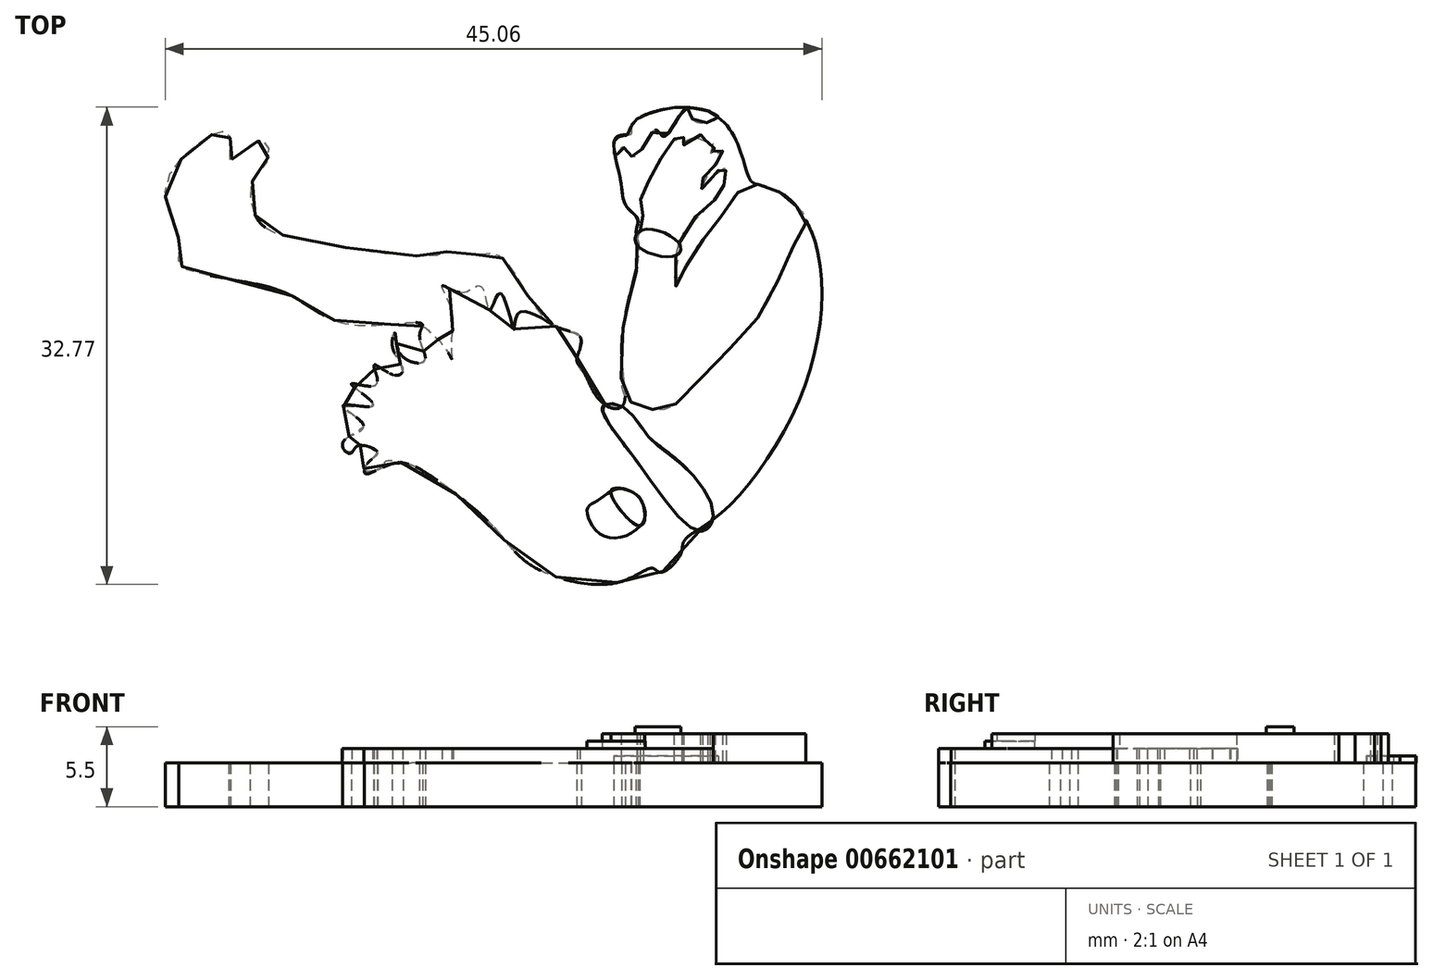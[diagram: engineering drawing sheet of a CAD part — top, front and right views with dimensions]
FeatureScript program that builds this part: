
annotation { "Feature Type Name" : "Feature", "Feature Type Description" : "" }
export const myFeature = defineFeature(function(context is Context, id is Id, definition is map)
    precondition{}
    {
        {
            var Q0;
            Q0=qCreatedBy(makeId("Top.planeOp"),FACE);
            var sketch = newSketch(context, id + "F0", { "sketchPlane" : qUnion([Q0])});
            skFitSpline(sketch, "E0", {"points": [v(-29.16, 38) * mm, v(-28.15, 38.22) * mm, v(-28.09, 38.84) * mm, v(-24.81, 40.03) * mm, v(-21.54, 38.73) * mm, v(-20.24, 35.68) * mm, v(-19.73, 34.83) * mm, v(-17.87, 34.15) * mm, v(-15.38, 30.26) * mm, v(-16.5, 20.2) * mm, v(-22.38, 11.84) * mm, v(-24.53, 10.26) * mm, v(-24.76, 9.36) * mm, v(-26.11, 8.11) * mm, v(-26.68, 8.4) * mm, v(-29, 7.44) * mm, v(-34.87, 8.5) * mm, v(-37.47, 11.1) * mm, v(-41.87, 14.72) * mm, v(-44.53, 15.57) * mm, v(-46.39, 14.9) * mm, v(-46.16, 15.68) * mm, v(-45.54, 16.36) * mm, v(-46.9, 16.81) * mm, v(-47.3, 16.36) * mm, v(-47.69, 16.36) * mm, v(-47.86, 17.15) * mm, v(-46.5, 18.17) * mm, v(-47.91, 19.58) * mm, v(-45.82, 19.58) * mm, v(-47.35, 21.05) * mm, v(-45.66, 21) * mm, v(-45.77, 22.35) * mm, v(-44.53, 21.67) * mm, v(-43.8, 22) * mm, v(-44.53, 23.6) * mm, v(-44.36, 24.55) * mm, v(-43.96, 23.08) * mm, v(-42.32, 22.63) * mm, v(-42.66, 24.38) * mm, v(-42.5, 25.17) * mm, v(-47.46, 25.12) * mm, v(-52.32, 27.49) * mm, v(-58.99, 29.13) * mm, v(-59.15, 30.76) * mm, v(-60.12, 34.38) * mm, v(-58.08, 37.37) * mm, v(-56.22, 38.39) * mm, v(-55.65, 37.94) * mm, v(-55.7, 36.47) * mm, v(-54.3, 37.43) * mm, v(-53.22, 37.65) * mm, v(-53.17, 36.24) * mm, v(-54.18, 34.89) * mm, v(-53.79, 32.35) * mm, v(-50.85, 30.99) * mm, v(-41.7, 29.86) * mm, v(-40.74, 30.14) * mm, v(-38.88, 29.92) * mm, v(-37.3, 29.92) * mm, v(-34.98, 26.7) * mm, v(-33.06, 24.89) * mm, v(-31.6, 24.16) * mm, v(-31.87, 22.69) * mm, v(-31.53, 22.12) * mm, v(-30.4, 20.03) * mm, v(-29.1, 19.35) * mm, v(-28.6, 19.86) * mm, v(-28.77, 24.21) * mm, v(-27.58, 30.42) * mm, v(-27.8, 31.5) * mm, v(-27.7, 32.35) * mm, v(-28.48, 33.25) * mm, v(-28.88, 35.06) * mm, v(-29.16, 38) * mm]});
            skSolve(sketch);
        }
        {
            var Q0;
            Q0 = qSketchRegion(id + "F0", true);
            extrude(context, id + "F1", {"entities" : qUnion([Q0]), "depth" : 3 * mm, "offsetDistance" : 25 * mm});
        }
        {
            var Q0;
            Q0=makeQuery(id+"F1.opExtrude","CAP_FACE",FACE,{"disambiguationData":[OSD([sQuery(id+"F0.wireOp",EDGE,"E0")])],"isStart":false});
            var sketch = newSketch(context, id + "F2", { "sketchPlane" : qUnion([Q0])});
            skFitSpline(sketch, "E1", {"points": [v(-28.78, 19.5) * mm, v(-27.21, 17.7) * mm, v(-24.55, 15.44) * mm, v(-22.58, 11.7) * mm, v(-24.42, 10.4) * mm, v(-24.96, 9.01) * mm, v(-26.25, 8.14) * mm, v(-26.75, 8.4) * mm, v(-28.1, 7.77) * mm, v(-30.53, 7.29) * mm, v(-32.45, 7.56) * mm, v(-34.31, 8.21) * mm, v(-36.12, 9.55) * mm, v(-37.99, 11.64) * mm, v(-39.73, 13.15) * mm, v(-41.44, 14.43) * mm, v(-43.41, 15.53) * mm, v(-45.06, 15.68) * mm, v(-45.18, 15.34) * mm, v(-46.45, 15.1) * mm, v(-45.96, 15.87) * mm, v(-45.6, 16.44) * mm, v(-46.35, 16.8) * mm, v(-46.92, 16.8) * mm, v(-47.22, 16.46) * mm, v(-47.81, 16.48) * mm, v(-47.88, 17.12) * mm, v(-46.5, 18.18) * mm, v(-47.04, 18.8) * mm, v(-47.9, 19.49) * mm, v(-46.12, 19.49) * mm, v(-45.91, 19.79) * mm, v(-47.32, 20.99) * mm, v(-46, 20.9) * mm, v(-45.55, 21.35) * mm, v(-45.77, 22.3) * mm, v(-44.35, 21.64) * mm, v(-43.83, 21.86) * mm, v(-44.35, 23.12) * mm, v(-44.5, 24.24) * mm, v(-44.42, 24.5) * mm, v(-44.04, 23.2) * mm, v(-42.75, 22.48) * mm, v(-42.27, 22.83) * mm, v(-42.63, 24.06) * mm, v(-42.5, 24.94) * mm, v(-42.47, 25.01) * mm, v(-40.92, 23.54) * mm, v(-40.45, 22.77) * mm, v(-40.45, 24.07) * mm, v(-40.45, 26.08) * mm, v(-41.1, 27.8) * mm, v(-39.74, 27.32) * mm, v(-38.44, 27.73) * mm, v(-37.85, 26.08) * mm, v(-37.14, 27.26) * mm, v(-36.2, 24.78) * mm, v(-35.9, 25.9) * mm, v(-33.54, 25.13) * mm, v(-32.32, 24.65) * mm, v(-31.69, 24.32) * mm, v(-31.85, 22.54) * mm, v(-31.24, 21.58) * mm, v(-30.12, 19.74) * mm, v(-28.78, 19.5) * mm]});
            skSolve(sketch);
        }
        {
            var Q0;
            Q0 = qSketchRegion(id + "F2", true);
            var Q1;
            {var subQ0=sQuery(id+"F2.wireOp",EDGE,"E1");var subQ1=makeQuery(id+"F1.opExtrude","CAP_EDGE",EDGE,{"disambiguationData":[OSD([sQuery(id+"F0.wireOp",EDGE,"E0")])],"isStart":false});var subQ47=makeQuery(id+"F2.imprint","INTERSECT",VERTEX,{"disambiguationData":[OD(0.0)],"derivedFrom":[subQ1,subQ0]});Q1=makeQuery(id+"F2.imprint","IMPRINT",FACE,{"disambiguationData":[TD([[makeQuery(id+"F2.imprint","IMPRINT",EDGE,{"disambiguationData":[TD([[subQ47,1.0]])],"derivedFrom":subQ0}),-1.0]])]});}
            extrude(context, id + "F3", {"entities" : qUnion([Q0, Q1]), "operationType" : NewBodyOperationType.ADD, "depth" : 1 * mm, "offsetDistance" : 25 * mm});
        }
        {
            var Q0;
            {var subQ0=sQuery(id+"F0.wireOp",EDGE,"E0");var subQ1=sQuery(id+"F2.wireOp",EDGE,"E1");Q0=makeQuery(id+"F3.boolean.opBoolean","SPLIT",FACE,{"disambiguationData":[TD([makeQuery(id+"F1.opExtrude","SWEPT_FACE",FACE,{"disambiguationData":[OSD([subQ0])]}),makeQuery(id+"F3.opExtrude","SWEPT_FACE",FACE,{"disambiguationData":[OSD([subQ1])]}),makeQuery(id+"F3.opExtrude","CAP_FACE",FACE,{"disambiguationData":[OSD([subQ1])],"isStart":true})]),OD(6.0)],"derivedFrom":makeQuery(id+"F1.opExtrude","CAP_FACE",FACE,{"disambiguationData":[OSD([subQ0])],"isStart":false})});}
            var sketch = newSketch(context, id + "F4", { "sketchPlane" : qUnion([Q0])});
            skFitSpline(sketch, "E2", {"points": [v(-27.7, 31.03) * mm, v(-27.32, 32.28) * mm, v(-27.53, 33.52) * mm, v(-26.66, 35.5) * mm, v(-25.05, 37.98) * mm, v(-24.56, 38.06) * mm, v(-24.68, 37.4) * mm, v(-23.4, 38.15) * mm, v(-22.9, 37.9) * mm, v(-23.24, 37.57) * mm, v(-22.7, 37.65) * mm, v(-22.4, 37.32) * mm, v(-22.74, 36.9) * mm, v(-22.08, 37.2) * mm, v(-21.87, 36.99) * mm, v(-22.57, 35.83) * mm, v(-23.4, 34.84) * mm, v(-23.24, 34.43) * mm, v(-22.74, 35.09) * mm, v(-22.16, 35.7) * mm, v(-21.7, 35.83) * mm, v(-21.7, 35.09) * mm, v(-22.24, 33.85) * mm, v(-24.68, 31.2) * mm, v(-25.05, 27.74) * mm, v(-24.06, 29.8) * mm, v(-22.53, 31.74) * mm, v(-20.92, 34.1) * mm, v(-19.57, 34.75) * mm, v(-18.04, 34.24) * mm, v(-16.84, 33.29) * mm, v(-16.15, 32.28) * mm, v(-17.04, 30.46) * mm, v(-19.19, 26) * mm, v(-22.74, 22.12) * mm, v(-25.55, 19.4) * mm, v(-27.16, 19.4) * mm, v(-28.56, 20.22) * mm, v(-28.78, 22.94) * mm, v(-28.74, 24.47) * mm, v(-28.51, 25.94) * mm, v(-27.76, 29.09) * mm, v(-27.7, 31.03) * mm]});
            skSolve(sketch);
        }
        {
            var Q0;
            Q0 = qSketchRegion(id + "F4", true);
            extrude(context, id + "F5", {"entities" : qUnion([Q0]), "operationType" : NewBodyOperationType.ADD, "depth" : 2 * mm, "offsetDistance" : 25 * mm});
        }
        {
            var Q0;
            Q0=makeQuery(id+"F5.opExtrude","CAP_FACE",FACE,{"disambiguationData":[OSD([sQuery(id+"F4.wireOp",EDGE,"E2")])],"isStart":false});
            var sketch = newSketch(context, id + "F6", { "sketchPlane" : qUnion([Q0])});
            skFitSpline(sketch, "E3", {"points": [v(-27.4, 31.62) * mm, v(-24.87, 30.7) * mm, v(-25.08, 29.86) * mm, v(-27.75, 30.6) * mm, v(-27.4, 31.62) * mm]});
            skSolve(sketch);
        }
        {
            var Q0;
            Q0 = qSketchRegion(id + "F6", true);
            extrude(context, id + "F7", {"entities" : qUnion([Q0]), "operationType" : NewBodyOperationType.ADD, "depth" : .5 * mm, "offsetDistance" : 25 * mm});
        }
        {
            var Q0;
            Q0=makeQuery(id+"F3.opExtrude","CAP_FACE",FACE,{"disambiguationData":[OSD([sQuery(id+"F2.wireOp",EDGE,"E1")])],"isStart":false});
            var sketch = newSketch(context, id + "F8", { "sketchPlane" : qUnion([Q0])});
            skFitSpline(sketch, "E4", {"points": [v(-30.08, 19.55) * mm, v(-27.65, 15.58) * mm, v(-23.48, 10.95) * mm, v(-22.51, 11.97) * mm, v(-24.23, 15.11) * mm, v(-26.9, 17.37) * mm, v(-28.64, 19.42) * mm, v(-30.08, 19.55) * mm]});
            skSolve(sketch);
        }
        {
            var Q0;
            Q0 = qSketchRegion(id + "F8", true);
            extrude(context, id + "F9", {"entities" : qUnion([Q0]), "operationType" : NewBodyOperationType.ADD, "depth" : 1 * mm, "offsetDistance" : 25 * mm});
        }
        {
            var Q0;
            Q0=makeQuery(id+"F9.boolean.opBoolean","SPLIT",FACE,{"disambiguationData":[OD(0.0)],"derivedFrom":makeQuery(id+"F3.opExtrude","CAP_FACE",FACE,{"disambiguationData":[OSD([sQuery(id+"F2.wireOp",EDGE,"E1")])],"isStart":false})});
            var sketch = newSketch(context, id + "F10", { "sketchPlane" : qUnion([Q0])});
            skFitSpline(sketch, "E5", {"points": [v(-28.73, 13.86) * mm, v(-27.2, 11.97) * mm, v(-29.81, 10.53) * mm, v(-31.17, 12.42) * mm, v(-30.44, 13.05) * mm, v(-28.73, 13.86) * mm]});
            skSolve(sketch);
        }
        {
            var Q0;
            Q0 = qSketchRegion(id + "F10", true);
            extrude(context, id + "F11", {"entities" : qUnion([Q0]), "operationType" : NewBodyOperationType.ADD, "depth" : .5 * mm, "offsetDistance" : 25 * mm});
        }
        {
            var Q0;
            Q0=makeQuery(id+"F11.opExtrude","CAP_FACE",FACE,{"disambiguationData":[OSD([sQuery(id+"F10.wireOp",EDGE,"E5")])],"isStart":false});
            var sketch = newSketch(context, id + "F12", { "sketchPlane" : qUnion([Q0])});
            skFitSpline(sketch, "E6", {"points": [v(-29.54, 13.67) * mm, v(-27.53, 11.3) * mm, v(-27.31, 12.72) * mm, v(-28.26, 13.71) * mm, v(-29.54, 13.67) * mm]});
            skSolve(sketch);
        }
        {
            var Q0;
            Q0 = qSketchRegion(id + "F12", true);
            extrude(context, id + "F13", {"entities" : qUnion([Q0]), "operationType" : NewBodyOperationType.ADD, "depth" : .5 * mm, "offsetDistance" : 25 * mm});
        }
        {
            var Q0;
            {var subQ0=sQuery(id+"F0.wireOp",EDGE,"E0");var subQ1=makeQuery(id+"F1.opExtrude","SWEPT_FACE",FACE,{"disambiguationData":[OSD([subQ0])]});var subQ2=sQuery(id+"F4.wireOp",EDGE,"E2");var subQ3=sQuery(id+"F2.wireOp",EDGE,"E1");Q0=makeQuery(id+"F5.boolean.opBoolean","SPLIT",FACE,{"disambiguationData":[TD([subQ1,makeQuery(id+"F5.opExtrude","SWEPT_FACE",FACE,{"disambiguationData":[OSD([subQ2])]}),makeQuery(id+"F5.opExtrude","CAP_FACE",FACE,{"disambiguationData":[OSD([subQ2])],"isStart":true})]),OD(3.0)],"derivedFrom":makeQuery(id+"F3.boolean.opBoolean","SPLIT",FACE,{"disambiguationData":[TD([subQ1,makeQuery(id+"F3.opExtrude","SWEPT_FACE",FACE,{"disambiguationData":[OSD([subQ3])]}),makeQuery(id+"F3.opExtrude","CAP_FACE",FACE,{"disambiguationData":[OSD([subQ3])],"isStart":true})]),OD(6.0)],"derivedFrom":makeQuery(id+"F1.opExtrude","CAP_FACE",FACE,{"disambiguationData":[OSD([subQ0])],"isStart":false})})});}
            var sketch = newSketch(context, id + "F14", { "sketchPlane" : qUnion([Q0])});
            skFitSpline(sketch, "E7", {"points": [v(-22.18, 39.38) * mm, v(-23.81, 39.08) * mm, v(-24.38, 40.03) * mm, v(-25.89, 38.04) * mm, v(-26.48, 38.49) * mm, v(-27.96, 36.63) * mm, v(-28.7, 37.3) * mm, v(-29.24, 36.65) * mm, v(-29.33, 37.45) * mm, v(-29.21, 37.94) * mm, v(-28.42, 38.16) * mm, v(-28.1, 38.83) * mm, v(-27.51, 39.37) * mm, v(-25.87, 39.9) * mm, v(-24.12, 40.01) * mm, v(-22.18, 39.38) * mm]});
            skSolve(sketch);
        }
        {
            var Q0;
            Q0 = qSketchRegion(id + "F14", true);
            extrude(context, id + "F15", {"entities" : qUnion([Q0]), "operationType" : NewBodyOperationType.ADD, "depth" : .5 * mm, "offsetDistance" : 25 * mm});
        }
    });
